# Revit family: Toilet-Siphon_Jet-Acorn-Dura-Ware-2120-3
name_source: partatom
category: Plumbing Fixtures
units: mm (PartAtom-declared; Revit-internal decimal feet)

## family parameters
Cut with Voids When Loaded = No
Host = Face
OmniClass Number = 23.45.05.21.11.11
OmniClass Title = Water Operated Water Closets
Part Type = Normal
Room Calculation Point = No
Round Connector Dimension = Use Diameter
Shared = Yes

## types (1)
- 2120-W-3
    -1.28 GPF (HET) = No
    -1.6 GPF (Not Available in California) = No
    -3.5 GPF (Not Available in California) = No
    -ADA 18” Integral Seat Height = No
    -BCN Blind Cap Nuts (4) = No
    -BL Bedpan Lugs = No
    -CN Cap Nuts (4) = No
    -EGE Enviro-Glaze Color Specify = No
    -FG 14 Gage Housing = No
    -FT Flood-Trol (N/A with Top Supply)** = No
    -FTA Flood-Trol Auto-Reset (N/A with Top Supply)** = No
    -FTE Flood-Trol Electronic** = No
    -FV Flush Valve, Mechanical (N/A for ADA) = No
    -FVBO Flush Valve by Other = No
    -FVH Flush Valve, Hydraulic (N/A for Top Supply) = No
    -FVL Flush Valve, ADA Lever Handle = No
    -FVT Flush Thru Wall Connector = No
    -HPS High Polish Integral Seat = No
    -HS-OFLC Hinged Seat, Open Front Less Cover = No
    -HS-OFWC Hinged Seat w/ Cover = No
    -MVCFV Time-Trol Flush Valve (N/A for Top Supply) = No
    -PFS Punched for Seat by Others = No
    -TF Transformer, 120VAC to 24VAC (-MVCFV option) = No
    -TSC Toilet Shipping Cover = No
    -VAC AcornVac System = No
    2120 Siphon Jet Toilet = Yes
    3 - On-Floor, Floor Outlet = Yes
    Assembly Code = D2010110
    CW Connection = Yes
    CWFU = 5
    Compliance Certifications = Comply with ASME A112.19.3- 2008 and CSA B45.4-2008 standards
    Default Elevation = 15"
    Description = Front Mount, On-Floor, Floor Waste, Siphon Jet, Stainless Steel Toilet
    Finish = Stainless Steel-Acorn-Satin
    Flush Rate = 1.28 GPF, 1.6 GPF or 3.5 GPF
    HW Connection = No
    HWFU = 0
    Height = 18 3/4"
    Inlet Connection Diameter = 1 1/2"
    Installation Type = Floor and Wall Supported
    Length = 29"
    Manufacturer = Acorn Engineering
    Material = Stainless Steel-Acorn-Satin
    Model = 2120-W-3
    Product Documentation Link = https://www.acorneng.com
    Product Page URL = https://www.acorneng.com
    Seat Height = 15"
    T - Top (Exposed) = No
    URL = https://www.acorneng.com
    Vent Connection = No
    W - Wall (Concealed) = Yes
    WFU = 5
    Waste Connection = Yes
    Waste Connection Diameter = 7 1/2"
    Width = 14"
    Working Pressure = minimum of 25 PSI flow pressure

## geometry (parser evidence)
native form markers: Sweep x3
no freeform markers — native parametric forms only
